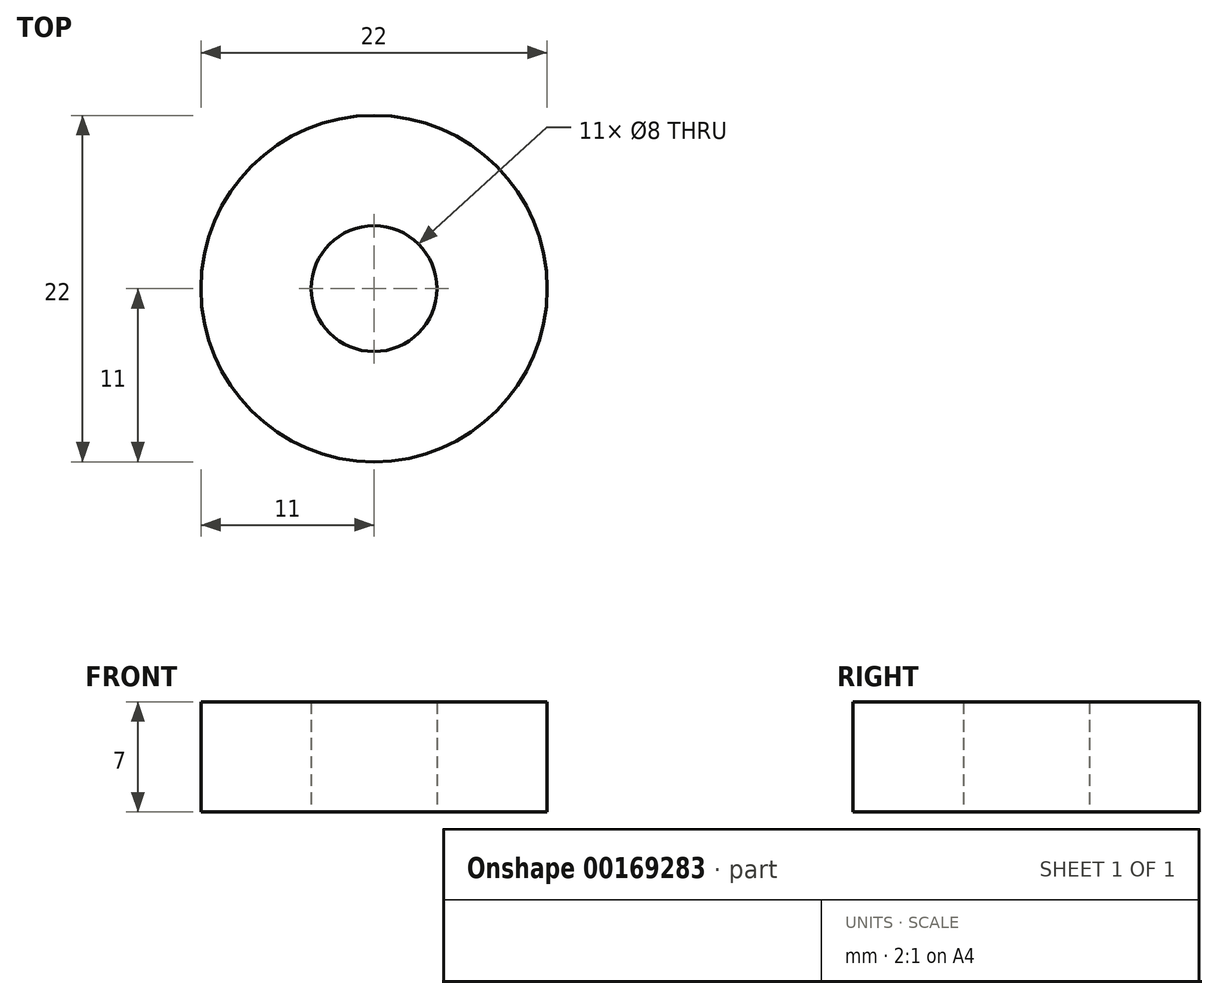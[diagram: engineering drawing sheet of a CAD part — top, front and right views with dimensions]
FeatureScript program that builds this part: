
annotation { "Feature Type Name" : "Feature", "Feature Type Description" : "" }
export const myFeature = defineFeature(function(context is Context, id is Id, definition is map)
    precondition{}
    {
        {
            var Q0;
            Q0=qCreatedBy(makeId("Top.planeOp"),FACE);
            var sketch = newSketch(context, id + "F0", { "sketchPlane" : qUnion([Q0])});
            skCircle(sketch, "E0", {"center": v(0, 0) * mm, "radius": 4 * mm});
            skCircle(sketch, "E1", {"center": v(0, 0) * mm, "radius": 11 * mm});
            skSolve(sketch);
        }
        {
            var Q0;
            Q0=makeQuery(id+"F0.imprint","IMPRINT",FACE,{"disambiguationData":[TD([[makeQuery(id+"F0.imprint","IMPRINT",EDGE,{"derivedFrom":sQuery(id+"F0.wireOp",EDGE,"E0")}),-1.0]])]});
            extrude(context, id + "F1", {"entities" : qUnion([Q0]), "depth" : 7 * mm});
        }
    });
